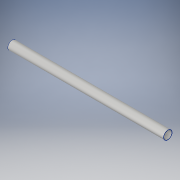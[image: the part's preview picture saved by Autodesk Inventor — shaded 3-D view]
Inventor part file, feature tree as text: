
AUTODESK INVENTOR PART (.ipt)
format: ipt  version: 2017 SP1 (Build 210196100, 196)  size: 97,280 bytes
history: native  units: in
note: dims shown in document units (in); Inventor stores cm internally (conversion verified against a paired STEP export)
features: revolve x1, shell x1, sketch x1
ambient origin geometry x8: Origin, YZ Plane, XZ Plane, XY Plane, X Axis, Y Axis, Z Axis, Center Point
bodies: Solid1 (feature_tree)
feature tree (3):
  revolve  "Revolution1"  [1 undecoded]
  shell  "Shell1"  Thickness=90.0deg
  sketch  "Sketch1"  dims[d0=4.0in d1=144.0in d2=90.0deg d3=0.25in]
note: 1 required parameter value undecoded (feature->parameter linkage not recoverable at this tier; creation-order binding heuristic only, values carry confidence <= 0.55)
